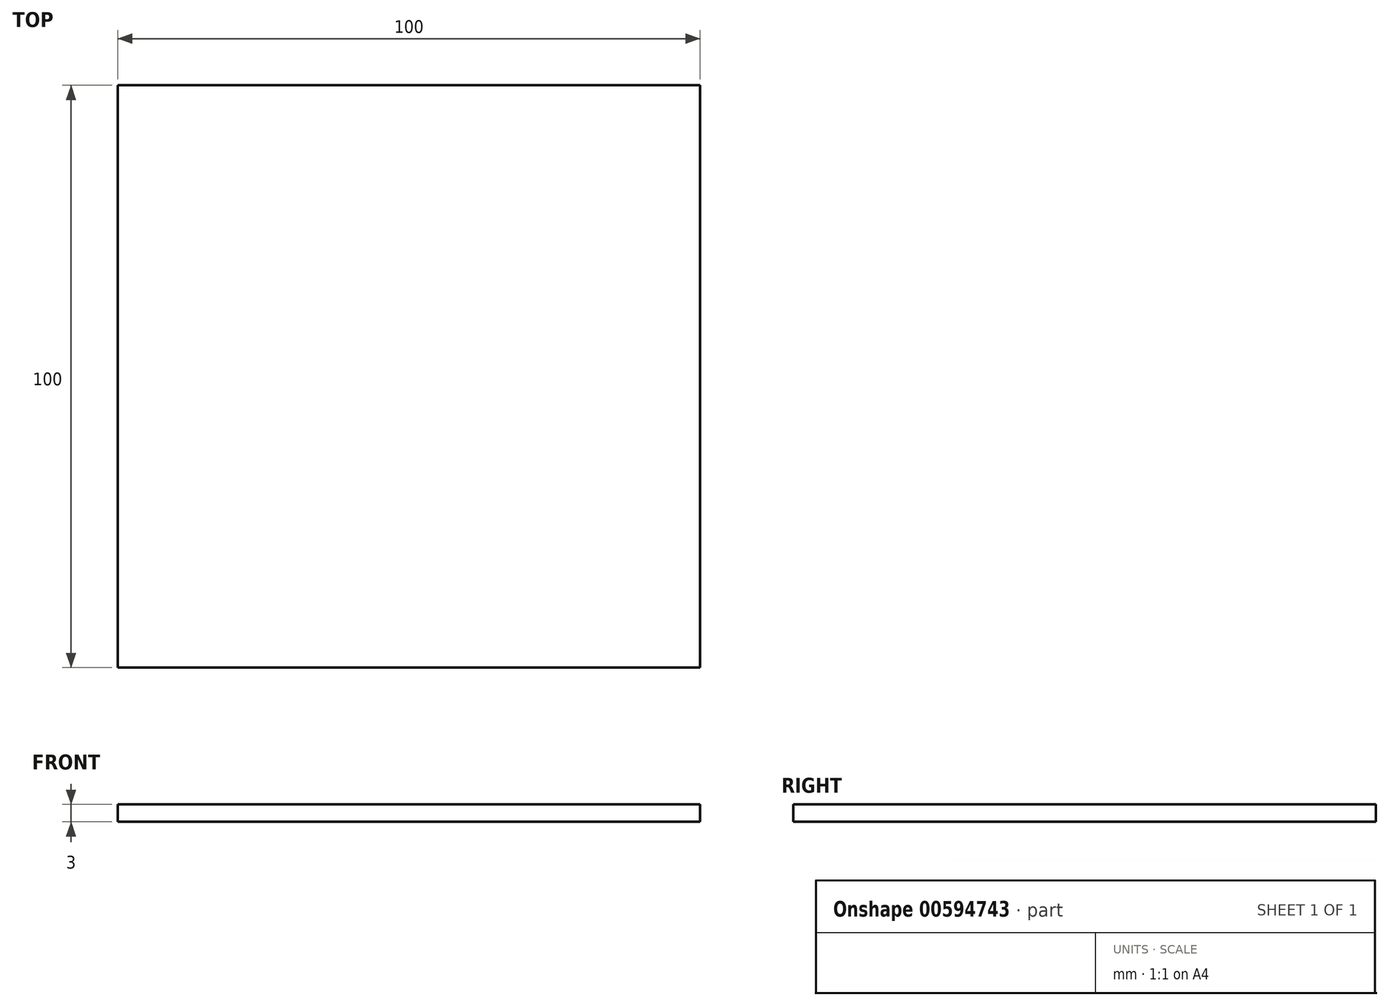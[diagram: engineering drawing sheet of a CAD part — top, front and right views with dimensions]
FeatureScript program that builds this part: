
annotation { "Feature Type Name" : "Feature", "Feature Type Description" : "" }
export const myFeature = defineFeature(function(context is Context, id is Id, definition is map)
    precondition{}
    {
        {
            var Q0;
            Q0=qCreatedBy(makeId("Top.planeOp"),FACE);
            var sketch = newSketch(context, id + "F0", { "sketchPlane" : qUnion([Q0])});
            skLineSegment(sketch, "E0.bottom", {"start": v(0, 0) * mm, "end": v(100, 0) * mm});
            skLineSegment(sketch, "E0.top", {"start": v(0, 100) * mm, "end": v(100, 100) * mm});
            skLineSegment(sketch, "E0.left", {"start": v(0, 0) * mm, "end": v(0, 100) * mm});
            skLineSegment(sketch, "E0.right", {"start": v(100, 0) * mm, "end": v(100, 100) * mm});
            skSolve(sketch);
        }
        {
            var Q0;
            Q0 = qSketchRegion(id + "F0", true);
            var Q1;
            Q1=makeQuery(id+"F0.imprint","IMPRINT",FACE,{"disambiguationData":[TD([[makeQuery(id+"F0.imprint","IMPRINT",EDGE,{"derivedFrom":sQuery(id+"F0.wireOp",EDGE,"E0.bottom")}),1.0]])]});
            extrude(context, id + "F1", {"entities" : qUnion([Q0, Q1]), "depth" : 3 * mm, "offsetDistance" : 25 * mm});
        }
    });
